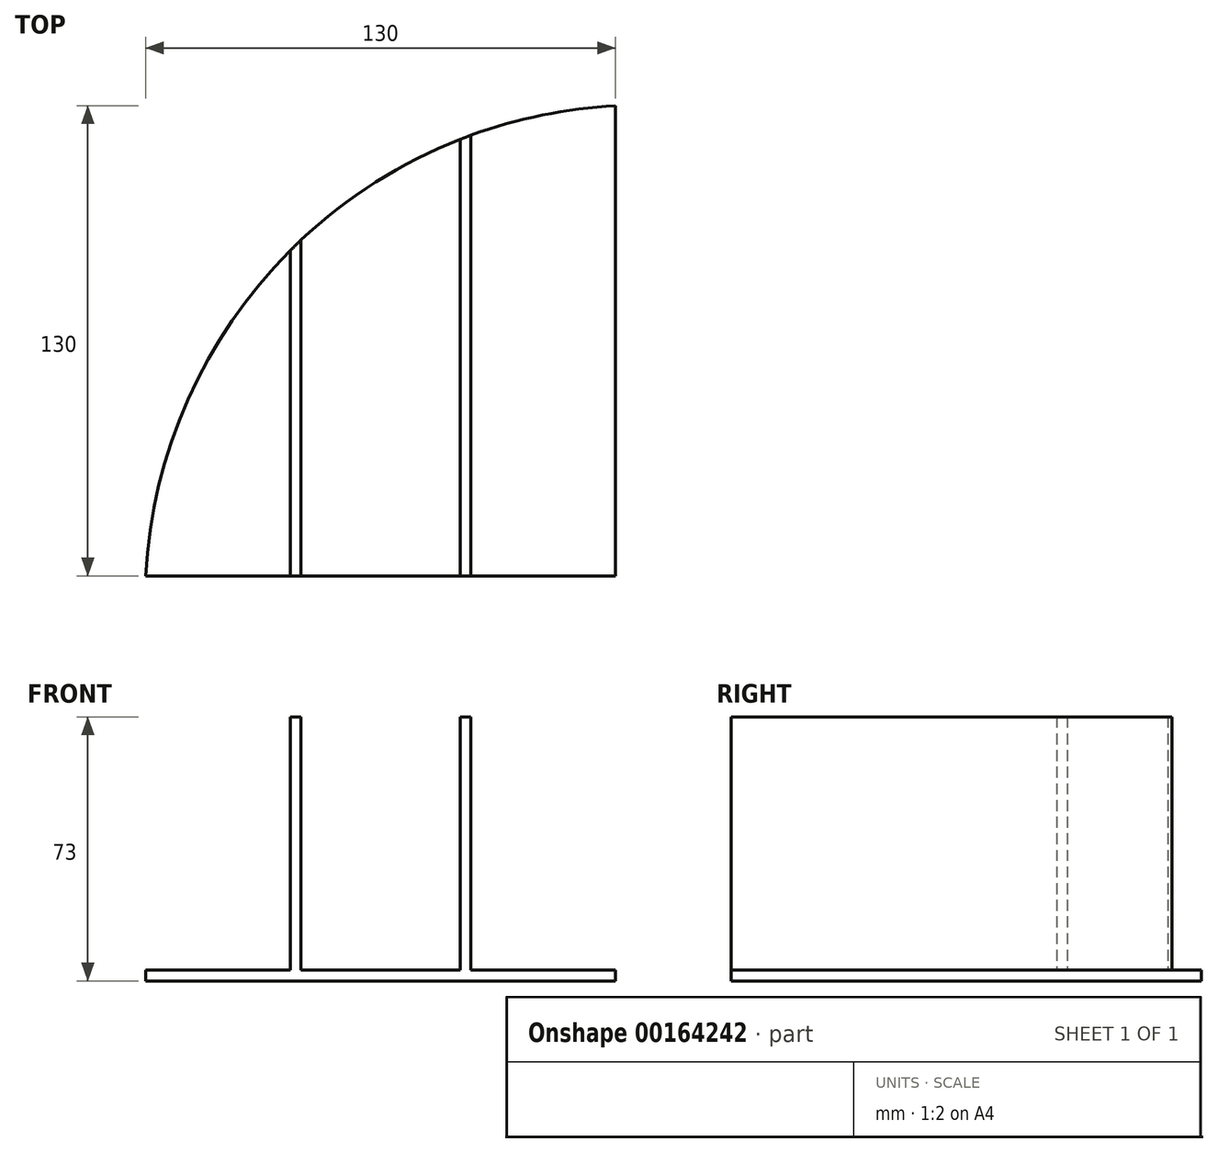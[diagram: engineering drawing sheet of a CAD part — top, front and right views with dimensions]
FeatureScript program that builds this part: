
annotation { "Feature Type Name" : "Feature", "Feature Type Description" : "" }
export const myFeature = defineFeature(function(context is Context, id is Id, definition is map)
    precondition{}
    {
        {
            var Q0;
            Q0=qCreatedBy(makeId("Top.planeOp"),FACE);
            var sketch = newSketch(context, id + "F0", { "sketchPlane" : qUnion([Q0])});
            skArc(sketch, "E0", {"start": v(101, 137.22) * mm, "mid": v(11.01, 97.2) * mm, "end": v(-29, 7.22) * mm});
            skLineSegment(sketch, "E1", {"start": v(101, 137.22) * mm, "end": v(101, 7.22) * mm});
            skLineSegment(sketch, "E2", {"start": v(101, 7.22) * mm, "end": v(-29, 7.22) * mm});
            skSolve(sketch);
        }
        {
            var Q0;
            Q0=makeQuery(id+"F0.imprint","IMPRINT",FACE,{"disambiguationData":[TD([[makeQuery(id+"F0.imprint","IMPRINT",EDGE,{"derivedFrom":sQuery(id+"F0.wireOp",EDGE,"E0")}),1.0]])]});
            extrude(context, id + "F1", {"entities" : qUnion([Q0]), "depth" : 3 * mm});
        }
        {
            var Q0;
            Q0=makeQuery(id+"F1.opExtrude","CAP_FACE",FACE,{"disambiguationData":[OSD([sQuery(id+"F0.wireOp",EDGE,"E0"),sQuery(id+"F0.wireOp",EDGE,"E1"),sQuery(id+"F0.wireOp",EDGE,"E2")])],"isStart":false});
            var sketch = newSketch(context, id + "F2", { "sketchPlane" : qUnion([Q0])});
            skLineSegment(sketch, "E3", {"start": v(11, 97.18) * mm, "end": v(11, 7.22) * mm});
            skLineSegment(sketch, "E4", {"start": v(11, 7.22) * mm, "end": v(14, 7.22) * mm});
            skLineSegment(sketch, "E5", {"start": v(14, 7.22) * mm, "end": v(14, 100.1) * mm});
            skLineSegment(sketch, "E6", {"start": v(58, 127.94) * mm, "end": v(58, 7.22) * mm});
            skLineSegment(sketch, "E7", {"start": v(58, 7.22) * mm, "end": v(61, 7.22) * mm});
            skLineSegment(sketch, "E8", {"start": v(61, 7.22) * mm, "end": v(61, 129.07) * mm});
            skSolve(sketch);
        }
        {
            var Q0;
            {var subQ0=sQuery(id+"F2.wireOp",EDGE,"E3");Q0=makeQuery(id+"F2.imprint","IMPRINT",FACE,{"disambiguationData":[TD([[makeQuery(id+"F2.imprint","IMPRINT",EDGE,{"derivedFrom":subQ0}),1.0]])]});}
            var Q1;
            {var subQ0=sQuery(id+"F2.wireOp",EDGE,"E6");Q1=makeQuery(id+"F2.imprint","IMPRINT",FACE,{"disambiguationData":[TD([[makeQuery(id+"F2.imprint","IMPRINT",EDGE,{"derivedFrom":subQ0}),1.0]])]});}
            extrude(context, id + "F3", {"entities" : qUnion([Q0, Q1]), "operationType" : NewBodyOperationType.ADD, "depth" : 70 * mm});
        }
    });
